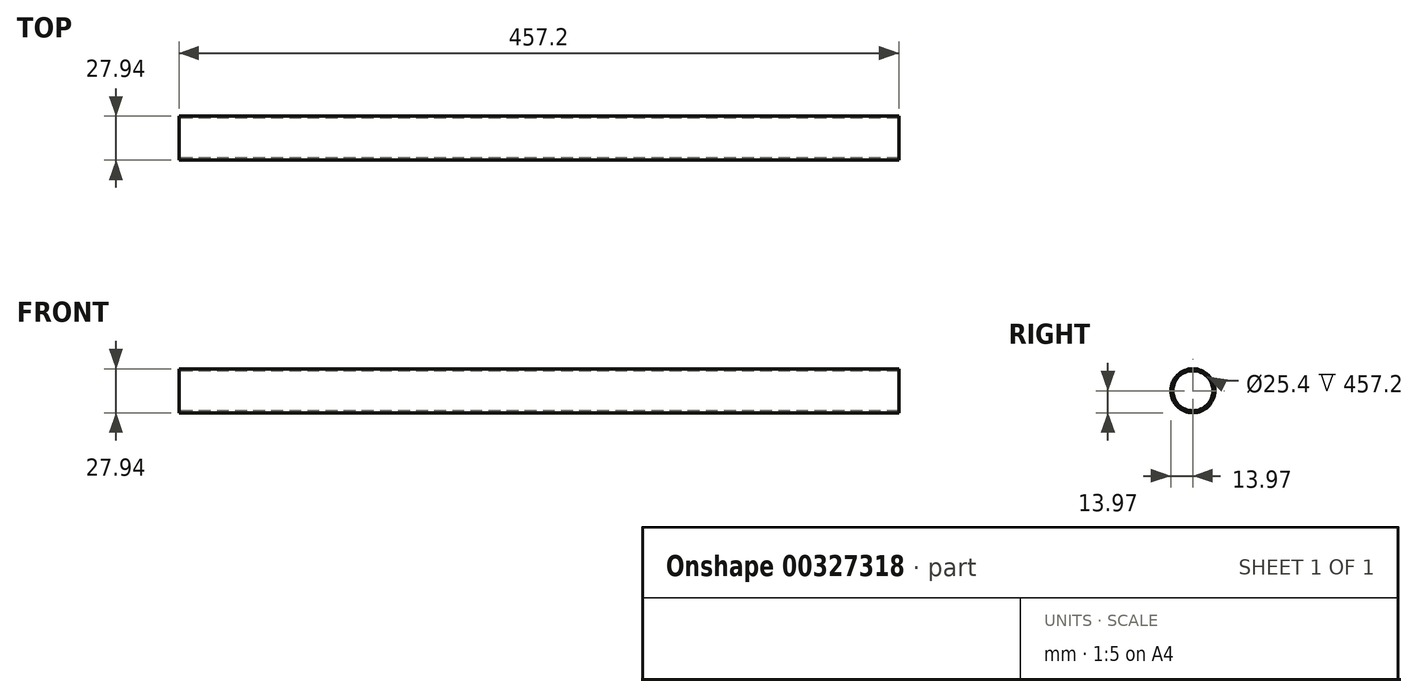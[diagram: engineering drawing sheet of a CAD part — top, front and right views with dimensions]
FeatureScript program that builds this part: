
annotation { "Feature Type Name" : "Feature", "Feature Type Description" : "" }
export const myFeature = defineFeature(function(context is Context, id is Id, definition is map)
    precondition{}
    {
        {
            var Q0;
            Q0=qCreatedBy(makeId("Right.planeOp"),FACE);
            var sketch = newSketch(context, id + "F0", { "sketchPlane" : qUnion([Q0])});
            skCircle(sketch, "E0", {"center": v(0, 0) * mm, "radius": 12.7 * mm});
            skCircle(sketch, "E1", {"center": v(0, 0) * mm, "radius": 13.97 * mm});
            skSolve(sketch);
        }
        {
            var Q0;
            Q0=makeQuery(id+"F0.imprint","IMPRINT",FACE,{"disambiguationData":[TD([[makeQuery(id+"F0.imprint","IMPRINT",EDGE,{"derivedFrom":sQuery(id+"F0.wireOp",EDGE,"E0")}),-1.0]])]});
            extrude(context, id + "F1", {"entities" : qUnion([Q0]), "depth" : 457.2 * mm});
        }
    });
